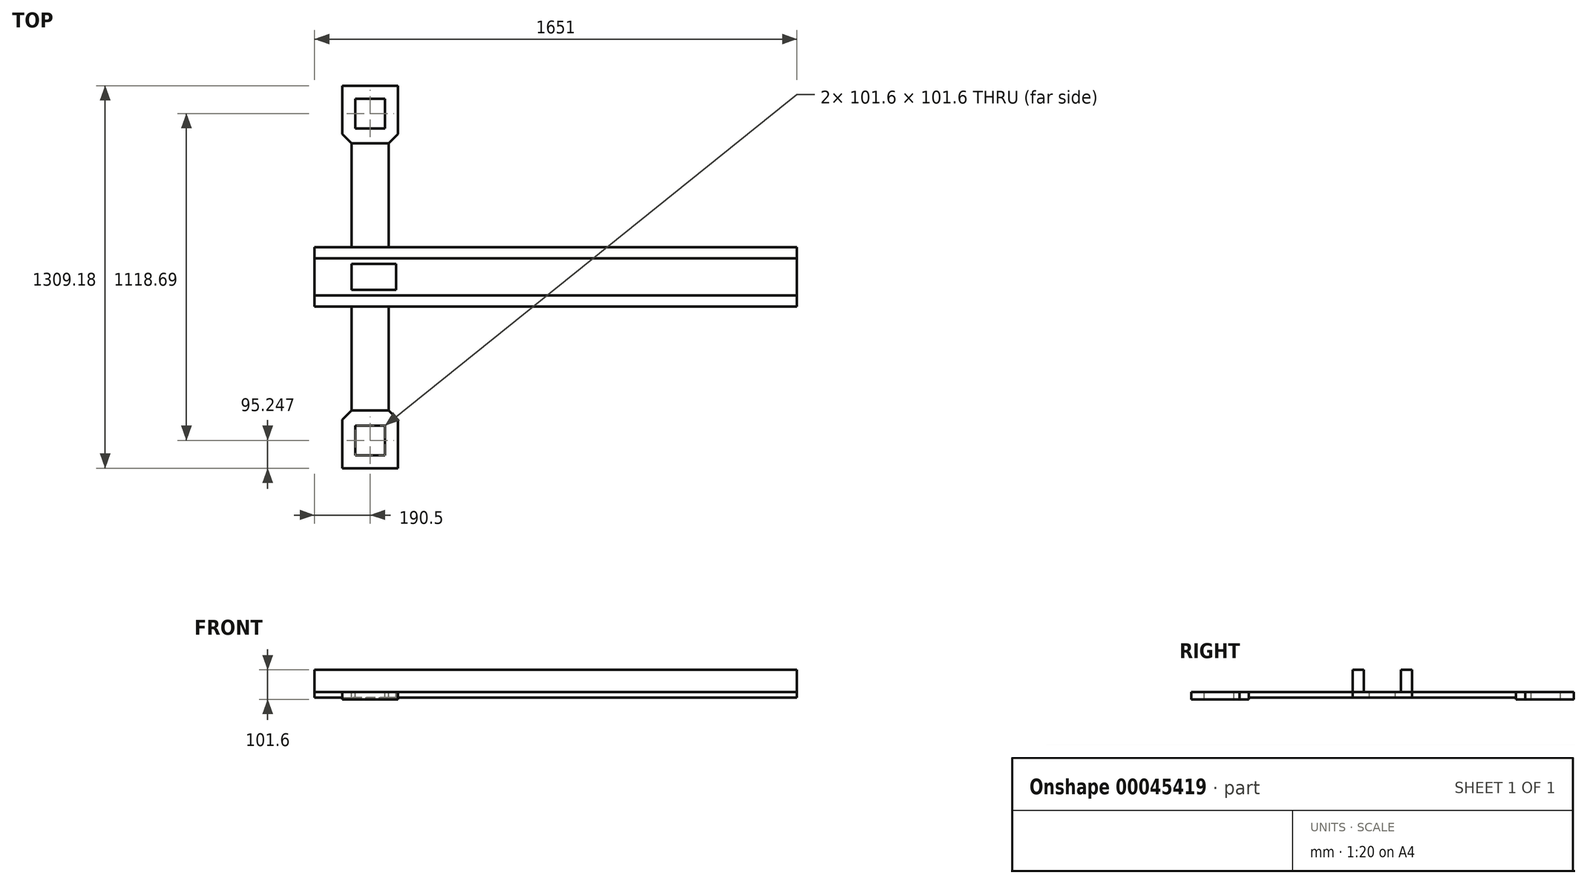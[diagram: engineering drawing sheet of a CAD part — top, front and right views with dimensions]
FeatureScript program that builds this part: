
annotation { "Feature Type Name" : "Feature", "Feature Type Description" : "" }
export const myFeature = defineFeature(function(context is Context, id is Id, definition is map)
    precondition{}
    {
        {
            var Q0;
            Q0=qCreatedBy(makeId("Top.planeOp"),FACE);
            var sketch = newSketch(context, id + "F0", { "sketchPlane" : qUnion([Q0])});
            skLineSegment(sketch, "E0.rect.bottom", {"start": v(825.5, 457.2) * mm, "end": v(-825.5, 457.2) * mm});
            skLineSegment(sketch, "E0.rect.top", {"start": v(825.5, -457.2) * mm, "end": v(-825.5, -457.2) * mm});
            skLineSegment(sketch, "E0.rect.left", {"start": v(825.5, 457.2) * mm, "end": v(825.5, -457.2) * mm});
            skLineSegment(sketch, "E0.rect.right", {"start": v(-825.5, 457.2) * mm, "end": v(-825.5, -457.2) * mm});
            skPoint(sketch, "E0.rect.middle", {"position": v(0, 0) * mm});
            skLineSegment(sketch, "E1", {"start": v(-825.5, 0) * mm, "end": v(-698.5, 0) * mm, "construction": true});
            skPoint(sketch, "E1.endSnap0", {"position": v(-825.5, 0) * mm});
            skLineSegment(sketch, "E2.rect.bottom", {"start": v(-698.5, 44.45) * mm, "end": v(-546.1, 44.45) * mm});
            skLineSegment(sketch, "E2.rect.top", {"start": v(-698.5, -44.45) * mm, "end": v(-546.1, -44.45) * mm});
            skLineSegment(sketch, "E2.rect.left", {"start": v(-698.5, 44.45) * mm, "end": v(-698.5, -44.45) * mm});
            skLineSegment(sketch, "E2.rect.right", {"start": v(-546.1, 44.45) * mm, "end": v(-546.1, -44.45) * mm});
            skPoint(sketch, "E2.rect.middle", {"position": v(-622.3, 0) * mm});
            skSolve(sketch);
        }
        {
            var Q0;
            Q0=makeQuery(id+"F0.imprint","IMPRINT",FACE,{"disambiguationData":[TD([[makeQuery(id+"F0.imprint","IMPRINT",EDGE,{"derivedFrom":sQuery(id+"F0.wireOp",EDGE,"E0.rect.bottom")}),1.0]])]});
            extrude(context, id + "F1", {"entities" : qUnion([Q0]), "oppositeDirection" : true, "depth" : 19.05 * mm});
        }
        {
            var Q0;
            Q0=makeQuery(id+"F1.opExtrude","SWEPT_FACE",FACE,{"disambiguationData":[OSD([sQuery(id+"F0.wireOp",EDGE,"E0.rect.left")])]});
            var sketch = newSketch(context, id + "F2", { "sketchPlane" : qUnion([Q0])});
            skLineSegment(sketch, "E3", {"start": v(0, 112.2) * mm, "end": v(0, -166.56) * mm, "construction": true});
            skLineSegment(sketch, "E4.bottom", {"start": v(-63.5, 0) * mm, "end": v(-101.6, 0) * mm});
            skLineSegment(sketch, "E4.top", {"start": v(-63.5, 76.2) * mm, "end": v(-101.6, 76.2) * mm});
            skLineSegment(sketch, "E4.left", {"start": v(-63.5, 0) * mm, "end": v(-63.5, 76.2) * mm});
            skLineSegment(sketch, "E4.right", {"start": v(-101.6, 0) * mm, "end": v(-101.6, 76.2) * mm});
            skLineSegment(sketch, "E5.MirrorCS", {"start": v(63.5, 0) * mm, "end": v(101.6, 0) * mm});
            skLineSegment(sketch, "E6.MirrorCS", {"start": v(101.6, 0) * mm, "end": v(101.6, 76.2) * mm});
            skLineSegment(sketch, "E7.MirrorCS", {"start": v(63.5, 76.2) * mm, "end": v(101.6, 76.2) * mm});
            skLineSegment(sketch, "E8.MirrorCS", {"start": v(63.5, 0) * mm, "end": v(63.5, 76.2) * mm});
            skSolve(sketch);
        }
        {
            var Q0;
            Q0=makeQuery(id+"F2.imprint","IMPRINT",FACE,{"disambiguationData":[TD([[makeQuery(id+"F2.imprint","IMPRINT",EDGE,{"derivedFrom":sQuery(id+"F2.wireOp",EDGE,"E4.bottom")}),-1.0]])]});
            var Q1;
            Q1=makeQuery(id+"F2.imprint","IMPRINT",FACE,{"disambiguationData":[TD([[makeQuery(id+"F2.imprint","IMPRINT",EDGE,{"derivedFrom":sQuery(id+"F2.wireOp",EDGE,"E5.MirrorCS")}),-1.0]])]});
            extrude(context, id + "F3", {"entities" : qUnion([Q0, Q1]), "oppositeDirection" : true, "depth" : 1651 * mm});
        }
        {
            var Q0;
            Q0=makeQuery(id+"F1.opExtrude","CAP_FACE",FACE,{"disambiguationData":[OSD([sQuery(id+"F0.wireOp",EDGE,"E0.rect.bottom"),sQuery(id+"F0.wireOp",EDGE,"E0.rect.top"),sQuery(id+"F0.wireOp",EDGE,"E0.rect.left"),sQuery(id+"F0.wireOp",EDGE,"E0.rect.right"),sQuery(id+"F0.wireOp",EDGE,"E2.rect.bottom"),sQuery(id+"F0.wireOp",EDGE,"E2.rect.top"),sQuery(id+"F0.wireOp",EDGE,"E2.rect.left"),sQuery(id+"F0.wireOp",EDGE,"E2.rect.right")])],"isStart":true});
            var sketch = newSketch(context, id + "F4", { "sketchPlane" : qUnion([Q0])});
            skLineSegment(sketch, "E9.bottom", {"start": v(825.5, -457.2) * mm, "end": v(-571.5, -457.2) * mm});
            skLineSegment(sketch, "E9.top", {"start": v(825.5, -101.6) * mm, "end": v(-571.5, -101.6) * mm});
            skLineSegment(sketch, "E9.left", {"start": v(825.5, -457.2) * mm, "end": v(825.5, -101.6) * mm});
            skLineSegment(sketch, "E9.right", {"start": v(-571.5, -457.2) * mm, "end": v(-571.5, -101.6) * mm});
            skLineSegment(sketch, "E10", {"start": v(-825.5, 0) * mm, "end": v(825.5, 0) * mm, "construction": true});
            skLineSegment(sketch, "E11.bottom", {"start": v(-825.5, -457.2) * mm, "end": v(-698.5, -457.2) * mm});
            skLineSegment(sketch, "E11.top", {"start": v(-825.5, -101.6) * mm, "end": v(-698.5, -101.6) * mm});
            skLineSegment(sketch, "E11.left", {"start": v(-825.5, -457.2) * mm, "end": v(-825.5, -101.6) * mm});
            skLineSegment(sketch, "E11.right", {"start": v(-698.5, -457.2) * mm, "end": v(-698.5, -101.6) * mm});
            skLineSegment(sketch, "E12.MirrorCS", {"start": v(825.5, 457.2) * mm, "end": v(825.5, 101.6) * mm});
            skLineSegment(sketch, "E13.MirrorCS", {"start": v(825.5, 101.6) * mm, "end": v(-571.5, 101.6) * mm});
            skLineSegment(sketch, "E14.MirrorCS", {"start": v(825.5, 457.2) * mm, "end": v(-571.5, 457.2) * mm});
            skLineSegment(sketch, "E15.MirrorCS", {"start": v(-571.5, 457.2) * mm, "end": v(-571.5, 101.6) * mm});
            skLineSegment(sketch, "E16.MirrorCS", {"start": v(-698.5, 457.2) * mm, "end": v(-698.5, 101.6) * mm});
            skLineSegment(sketch, "E17.MirrorCS", {"start": v(-825.5, 457.2) * mm, "end": v(-698.5, 457.2) * mm});
            skLineSegment(sketch, "E18.MirrorCS", {"start": v(-825.5, 101.6) * mm, "end": v(-698.5, 101.6) * mm});
            skLineSegment(sketch, "E19.MirrorCS", {"start": v(-825.5, 457.2) * mm, "end": v(-825.5, 101.6) * mm});
            skSolve(sketch);
        }
        {
            var Q0;
            Q0 = qSketchRegion(id + "F4", true);
            extrude(context, id + "F5", {"entities" : qUnion([Q0]), "operationType" : NewBodyOperationType.REMOVE, "endBound" : BoundingType.THROUGH_ALL, "oppositeDirection" : true, "depth" : 25.4 * mm});
        }
        {
            var Q0;
            Q0=makeQuery(id+"F1.opExtrude","CAP_FACE",FACE,{"disambiguationData":[OSD([sQuery(id+"F0.wireOp",EDGE,"E0.rect.bottom"),sQuery(id+"F0.wireOp",EDGE,"E0.rect.top"),sQuery(id+"F0.wireOp",EDGE,"E0.rect.left"),sQuery(id+"F0.wireOp",EDGE,"E0.rect.right"),sQuery(id+"F0.wireOp",EDGE,"E2.rect.bottom"),sQuery(id+"F0.wireOp",EDGE,"E2.rect.top"),sQuery(id+"F0.wireOp",EDGE,"E2.rect.left"),sQuery(id+"F0.wireOp",EDGE,"E2.rect.right")])],"isStart":true});
            var sketch = newSketch(context, id + "F6", { "sketchPlane" : qUnion([Q0])});
            skLineSegment(sketch, "E20", {"start": v(-698.5, -457.2) * mm, "end": v(-730.25, -488.95) * mm});
            skLineSegment(sketch, "E21", {"start": v(-730.25, -488.95) * mm, "end": v(-730.25, -654.6) * mm});
            skLineSegment(sketch, "E22", {"start": v(-635, -457.2) * mm, "end": v(-635, -661.49) * mm, "construction": true});
            skLineSegment(sketch, "E23.rect.bottom", {"start": v(-685.8, -508.54) * mm, "end": v(-584.2, -508.54) * mm});
            skLineSegment(sketch, "E23.rect.top", {"start": v(-685.8, -610.14) * mm, "end": v(-584.2, -610.14) * mm});
            skLineSegment(sketch, "E23.rect.left", {"start": v(-685.8, -508.54) * mm, "end": v(-685.8, -610.14) * mm});
            skLineSegment(sketch, "E23.rect.right", {"start": v(-584.2, -508.54) * mm, "end": v(-584.2, -610.14) * mm});
            skPoint(sketch, "E23.rect.middle", {"position": v(-635, -559.34) * mm});
            skLineSegment(sketch, "E24", {"start": v(-730.25, -654.6) * mm, "end": v(-539.75, -654.6) * mm});
            skLineSegment(sketch, "E25.MirrorCS", {"start": v(-571.5, -457.2) * mm, "end": v(-539.75, -488.95) * mm});
            skLineSegment(sketch, "E26.MirrorCS", {"start": v(-539.75, -488.95) * mm, "end": v(-539.75, -654.6) * mm});
            skLineSegment(sketch, "E27", {"start": v(-825.5, 0) * mm, "end": v(825.5, 0) * mm, "construction": true});
            skLineSegment(sketch, "E28", {"start": v(-698.5, -457.2) * mm, "end": v(-571.5, -457.2) * mm, "construction": true});
            skLineSegment(sketch, "E29.MirrorCS", {"start": v(-698.5, 457.2) * mm, "end": v(-730.25, 488.95) * mm});
            skLineSegment(sketch, "E30.MirrorCS", {"start": v(-571.5, 457.2) * mm, "end": v(-539.75, 488.95) * mm});
            skLineSegment(sketch, "E31.MirrorCS", {"start": v(-685.8, 508.54) * mm, "end": v(-584.2, 508.54) * mm});
            skLineSegment(sketch, "E32.MirrorCS", {"start": v(-685.8, 508.54) * mm, "end": v(-685.8, 610.14) * mm});
            skLineSegment(sketch, "E33.MirrorCS", {"start": v(-539.75, 488.95) * mm, "end": v(-539.75, 654.6) * mm});
            skLineSegment(sketch, "E34.MirrorCS", {"start": v(-730.25, 488.95) * mm, "end": v(-730.25, 654.6) * mm});
            skPoint(sketch, "E35.MirrorP", {"position": v(-635, 559.34) * mm});
            skLineSegment(sketch, "E36.MirrorCS", {"start": v(-635, 457.2) * mm, "end": v(-635, 661.49) * mm, "construction": true});
            skLineSegment(sketch, "E37.MirrorCS", {"start": v(-698.5, 457.2) * mm, "end": v(-571.5, 457.2) * mm, "construction": true});
            skLineSegment(sketch, "E38.MirrorCS", {"start": v(-685.8, 610.14) * mm, "end": v(-584.2, 610.14) * mm});
            skLineSegment(sketch, "E39.MirrorCS", {"start": v(-584.2, 508.54) * mm, "end": v(-584.2, 610.14) * mm});
            skLineSegment(sketch, "E40.MirrorCS", {"start": v(-730.25, 654.6) * mm, "end": v(-539.75, 654.6) * mm});
            skSolve(sketch);
        }
        {
            var Q0;
            Q0=makeQuery(id+"F6.imprint","IMPRINT",FACE,{"disambiguationData":[TD([[makeQuery(id+"F6.imprint","IMPRINT",EDGE,{"derivedFrom":sQuery(id+"F6.wireOp",EDGE,"E20")}),1.0]])]});
            var Q1;
            Q1=makeQuery(id+"F6.imprint","IMPRINT",FACE,{"disambiguationData":[TD([[makeQuery(id+"F6.imprint","IMPRINT",EDGE,{"derivedFrom":sQuery(id+"F6.wireOp",EDGE,"E29.MirrorCS")}),-1.0]])]});
            extrude(context, id + "F7", {"entities" : qUnion([Q0, Q1]), "oppositeDirection" : true, "depth" : 25.4 * mm});
        }
    });
